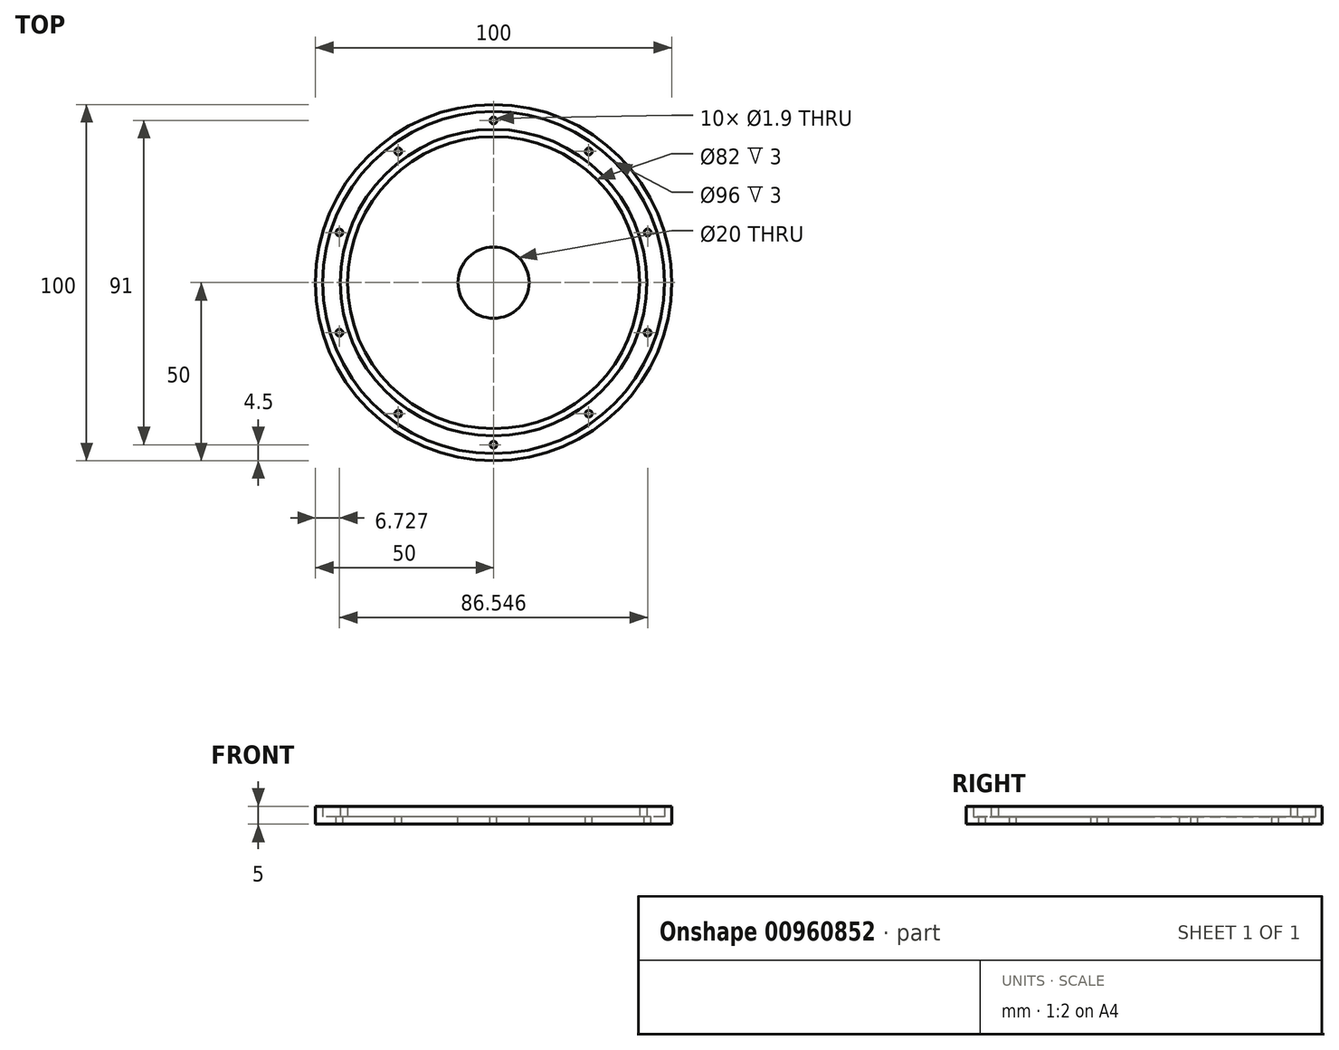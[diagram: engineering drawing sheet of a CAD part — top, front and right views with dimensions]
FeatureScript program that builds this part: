
annotation { "Feature Type Name" : "Feature", "Feature Type Description" : "" }
export const myFeature = defineFeature(function(context is Context, id is Id, definition is map)
    precondition{}
    {
        {
            var Q0;
            Q0=qCreatedBy(makeId("Top.planeOp"),FACE);
            var sketch = newSketch(context, id + "F0", { "sketchPlane" : qUnion([Q0])});
            skCircle(sketch, "E0", {"center": v(0, 0) * mm, "radius": 50 * mm});
            skSolve(sketch);
        }
        {
            var Q0;
            Q0 = qSketchRegion(id + "F0", true);
            extrude(context, id + "F1", {"entities" : qUnion([Q0]), "depth" : 2 * mm, "offsetDistance" : 25 * mm});
        }
        {
            var Q0;
            Q0=makeQuery(id+"F1.opExtrude","CAP_FACE",FACE,{"disambiguationData":[OSD([sQuery(id+"F0.wireOp",EDGE,"E0")])],"isStart":false});
            var sketch = newSketch(context, id + "F2", { "sketchPlane" : qUnion([Q0])});
            skCircle(sketch, "E1", {"center": v(0, 0) * mm, "radius": 41 * mm});
            skCircle(sketch, "E2", {"center": v(0, 0) * mm, "radius": 43 * mm});
            skCircle(sketch, "E3", {"center": v(0, 0) * mm, "radius": 48 * mm});
            skSolve(sketch);
        }
        {
            var Q0;
            Q0=makeQuery(id+"F2.imprint","IMPRINT",FACE,{"disambiguationData":[TD([[makeQuery(id+"F2.imprint","IMPRINT",EDGE,{"derivedFrom":sQuery(id+"F2.wireOp",EDGE,"E1")}),-1.0]])]});
            var Q1;
            Q1=makeQuery(id+"F2.imprint","IMPRINT",FACE,{"disambiguationData":[TD([[makeQuery(id+"F2.imprint","IMPRINT",EDGE,{"derivedFrom":sQuery(id+"F2.wireOp",EDGE,"E3")}),-1.0]])]});
            extrude(context, id + "F3", {"entities" : qUnion([Q0, Q1]), "operationType" : NewBodyOperationType.ADD, "depth" : 3 * mm, "offsetDistance" : 25 * mm});
        }
        {
            var Q0;
            Q0=makeQuery(id+"F3.boolean.opBoolean","SPLIT",FACE,{"disambiguationData":[TD([makeQuery(id+"F3.opExtrude","SWEPT_FACE",FACE,{"disambiguationData":[OSD([sQuery(id+"F2.wireOp",EDGE,"E2")])]})])],"derivedFrom":makeQuery(id+"F1.opExtrude","CAP_FACE",FACE,{"disambiguationData":[OSD([sQuery(id+"F0.wireOp",EDGE,"E0")])],"isStart":false})});
            var sketch = newSketch(context, id + "F4", { "sketchPlane" : qUnion([Q0])});
            skCircle(sketch, "E4", {"center": v(0, 45.5) * mm, "radius": 0.95 * mm});
            skCircle(sketch, "E5.1.0", {"center": v(-26.74, 36.81) * mm, "radius": 0.95 * mm});
            skCircle(sketch, "E5.2.0", {"center": v(-43.27, 14.06) * mm, "radius": 0.95 * mm});
            skCircle(sketch, "E5.3.0", {"center": v(-43.27, -14.06) * mm, "radius": 0.95 * mm});
            skCircle(sketch, "E5.4.0", {"center": v(-26.74, -36.81) * mm, "radius": 0.95 * mm});
            skCircle(sketch, "E5.5.0", {"center": v(0, -45.5) * mm, "radius": 0.95 * mm});
            skCircle(sketch, "E5.6.0", {"center": v(26.74, -36.81) * mm, "radius": 0.95 * mm});
            skCircle(sketch, "E5.7.0", {"center": v(43.27, -14.06) * mm, "radius": 0.95 * mm});
            skCircle(sketch, "E5.8.0", {"center": v(43.27, 14.06) * mm, "radius": 0.95 * mm});
            skCircle(sketch, "E5.9.0", {"center": v(26.74, 36.81) * mm, "radius": 0.95 * mm});
            skPoint(sketch, "E5.center", {"position": v(0, 0) * mm});
            skSolve(sketch);
        }
        {
            var Q0;
            Q0 = qSketchRegion(id + "F4", true);
            extrude(context, id + "F5", {"entities" : qUnion([Q0]), "operationType" : NewBodyOperationType.REMOVE, "endBound" : BoundingType.THROUGH_ALL, "oppositeDirection" : true, "depth" : 25 * mm, "offsetDistance" : 25 * mm});
        }
        {
            var Q0;
            Q0=makeQuery(id+"F3.boolean.opBoolean","SPLIT",FACE,{"disambiguationData":[TD([makeQuery(id+"F3.opExtrude","SWEPT_FACE",FACE,{"disambiguationData":[OSD([sQuery(id+"F2.wireOp",EDGE,"E1")])]})])],"derivedFrom":makeQuery(id+"F1.opExtrude","CAP_FACE",FACE,{"disambiguationData":[OSD([sQuery(id+"F0.wireOp",EDGE,"E0")])],"isStart":false})});
            var sketch = newSketch(context, id + "F6", { "sketchPlane" : qUnion([Q0])});
            skCircle(sketch, "E6", {"center": v(0, 0) * mm, "radius": 10 * mm});
            skSolve(sketch);
        }
        {
            var Q0;
            Q0=makeQuery(id+"F6.imprint","IMPRINT",FACE,{"disambiguationData":[TD([[makeQuery(id+"F6.imprint","IMPRINT",EDGE,{"derivedFrom":sQuery(id+"F6.wireOp",EDGE,"E6")}),1.0]])]});
            extrude(context, id + "F7", {"entities" : qUnion([Q0]), "operationType" : NewBodyOperationType.REMOVE, "endBound" : BoundingType.THROUGH_ALL, "oppositeDirection" : true, "depth" : 25 * mm, "offsetDistance" : 25 * mm});
        }
    });
